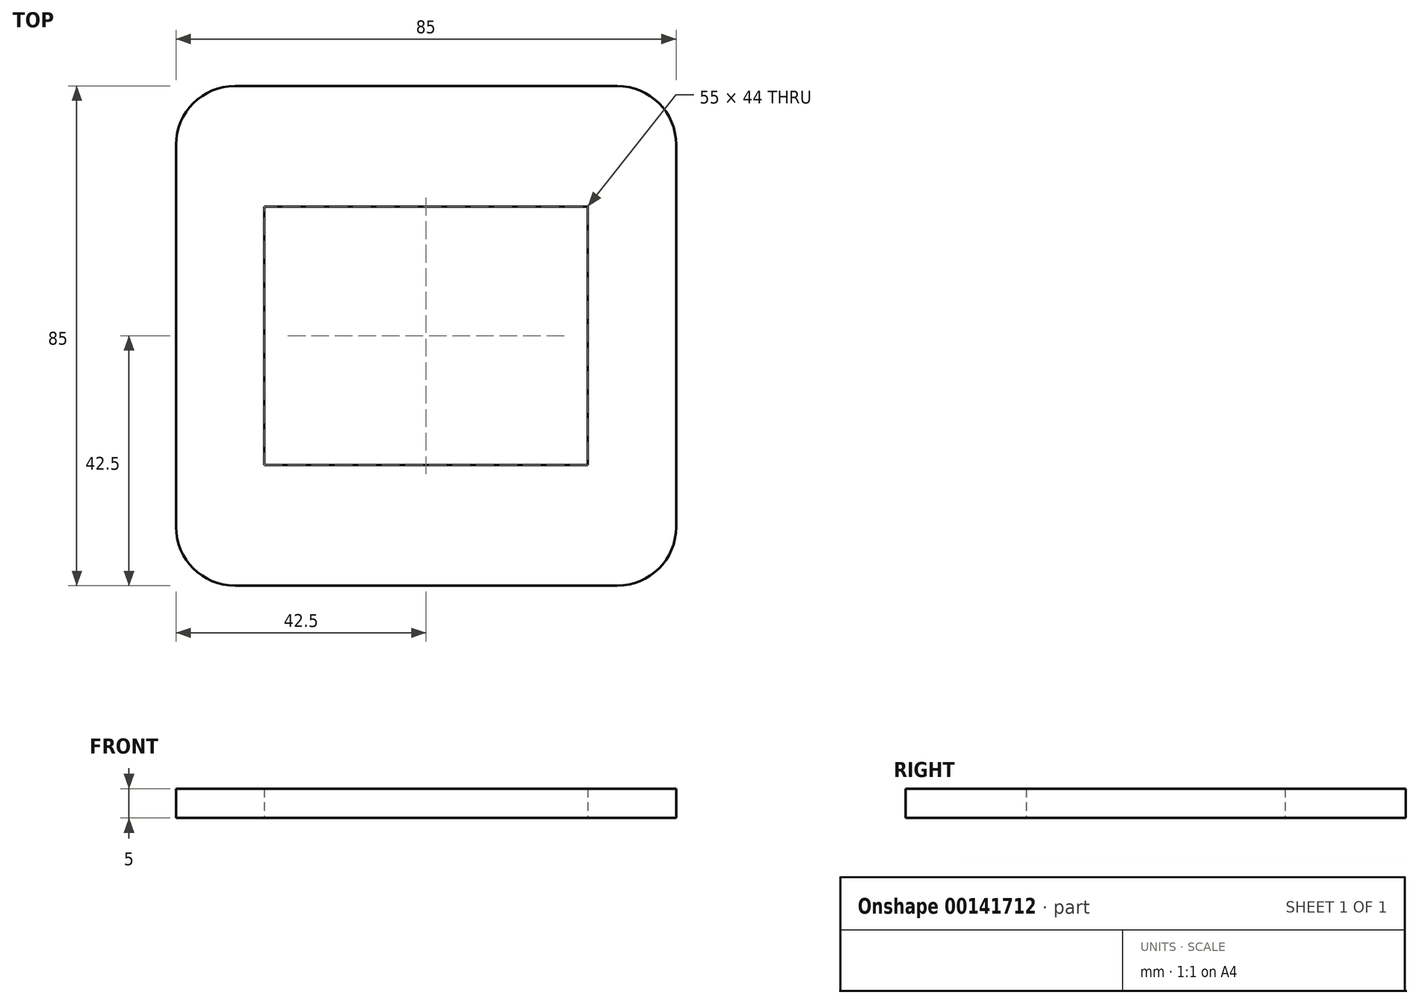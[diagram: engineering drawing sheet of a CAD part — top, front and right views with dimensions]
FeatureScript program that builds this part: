
annotation { "Feature Type Name" : "Feature", "Feature Type Description" : "" }
export const myFeature = defineFeature(function(context is Context, id is Id, definition is map)
    precondition{}
    {
        {
            var Q0;
            Q0=qCreatedBy(makeId("Top.planeOp"),FACE);
            var sketch = newSketch(context, id + "F0", { "sketchPlane" : qUnion([Q0])});
            skLineSegment(sketch, "E0.bottom", {"start": v(-32.5, 42.5) * mm, "end": v(32.5, 42.5) * mm});
            skLineSegment(sketch, "E0.top", {"start": v(-32.5, -42.5) * mm, "end": v(32.5, -42.5) * mm});
            skLineSegment(sketch, "E0.left", {"start": v(-42.5, 32.5) * mm, "end": v(-42.5, -32.5) * mm});
            skLineSegment(sketch, "E0.right", {"start": v(42.5, 32.5) * mm, "end": v(42.5, -32.5) * mm});
            skPoint(sketch, "E1.visualSharp", {"position": v(-42.5, 42.5) * mm});
            skArc(sketch, "E1.filletArc", {"start": v(-32.5, 42.5) * mm, "mid": v(-39.57, 39.57) * mm, "end": v(-42.5, 32.5) * mm});
            skPoint(sketch, "E2.visualSharp", {"position": v(42.5, 42.5) * mm});
            skArc(sketch, "E2.filletArc", {"start": v(42.5, 32.5) * mm, "mid": v(39.57, 39.57) * mm, "end": v(32.5, 42.5) * mm});
            skPoint(sketch, "E3.visualSharp", {"position": v(42.5, -42.5) * mm});
            skArc(sketch, "E3.filletArc", {"start": v(32.5, -42.5) * mm, "mid": v(39.57, -39.57) * mm, "end": v(42.5, -32.5) * mm});
            skPoint(sketch, "E4.visualSharp", {"position": v(-42.5, -42.5) * mm});
            skArc(sketch, "E4.filletArc", {"start": v(-42.5, -32.5) * mm, "mid": v(-39.57, -39.57) * mm, "end": v(-32.5, -42.5) * mm});
            skLineSegment(sketch, "E5.bottom", {"start": v(-27.5, 22) * mm, "end": v(27.5, 22) * mm});
            skLineSegment(sketch, "E5.top", {"start": v(-27.5, -22) * mm, "end": v(27.5, -22) * mm});
            skLineSegment(sketch, "E5.left", {"start": v(-27.5, 22) * mm, "end": v(-27.5, -22) * mm});
            skLineSegment(sketch, "E5.right", {"start": v(27.5, 22) * mm, "end": v(27.5, -22) * mm});
            skSolve(sketch);
        }
        {
            var Q0;
            Q0=qSketchRegion(id+"F0",true);
            extrude(context, id + "F1", {"entities" : qUnion([Q0]), "depth" : 5 * mm});
        }
    });
